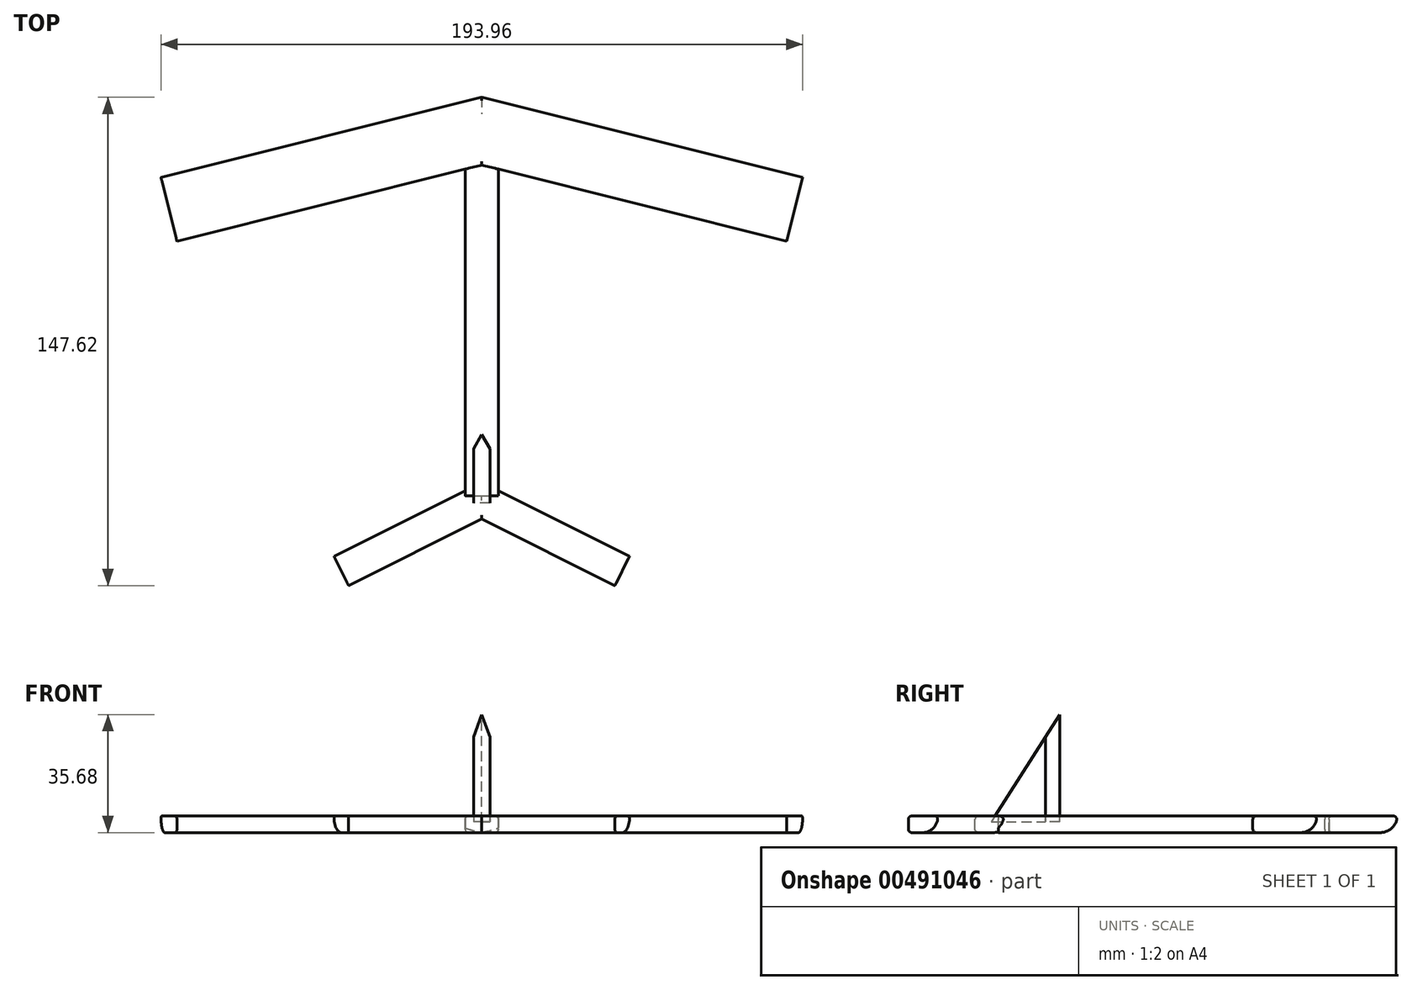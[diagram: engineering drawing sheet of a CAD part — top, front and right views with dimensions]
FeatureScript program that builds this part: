
annotation { "Feature Type Name" : "Feature", "Feature Type Description" : "" }
export const myFeature = defineFeature(function(context is Context, id is Id, definition is map)
    precondition{}
    {
        {
            var Q0;
            Q0=qCreatedBy(makeId("Top.planeOp"),FACE);
            var sketch = newSketch(context, id + "F0", { "sketchPlane" : qUnion([Q0])});
            skLineSegment(sketch, "E0", {"start": v(0, 0) * mm, "end": v(97.01, -24.25) * mm});
            skLineSegment(sketch, "E1", {"start": v(97.01, -24.25) * mm, "end": v(92.16, -43.66) * mm});
            skLineSegment(sketch, "E2", {"start": v(92.16, -43.66) * mm, "end": v(0, -20.62) * mm});
            skLineSegment(sketch, "E3", {"start": v(0, -20.62) * mm, "end": v(0, 0) * mm});
            skPoint(sketch, "E4.start.orphan", {"position": v(-0.68, 0) * mm});
            skLineSegment(sketch, "E5", {"start": v(0, 0) * mm, "end": v(-97.01, -24.25) * mm});
            skLineSegment(sketch, "E6", {"start": v(-97.01, -24.25) * mm, "end": v(-92.16, -43.66) * mm});
            skLineSegment(sketch, "E7", {"start": v(-92.16, -43.66) * mm, "end": v(0, -20.62) * mm});
            skSolve(sketch);
        }
        {
            var Q0;
            Q0=makeQuery(id+"F0.imprint","IMPRINT",FACE,{"disambiguationData":[TD([[makeQuery(id+"F0.imprint","IMPRINT",EDGE,{"derivedFrom":sQuery(id+"F0.wireOp",EDGE,"E0")}),-1.0]])]});
            extrude(context, id + "F1", {"entities" : qUnion([Q0]), "depth" : 5 * mm});
        }
        {
            var Q0;
            Q0=makeQuery(id+"F0.imprint","IMPRINT",FACE,{"disambiguationData":[TD([[makeQuery(id+"F0.imprint","IMPRINT",EDGE,{"derivedFrom":sQuery(id+"F0.wireOp",EDGE,"E3")}),1.0]])]});
            extrude(context, id + "F2", {"entities" : qUnion([Q0]), "operationType" : NewBodyOperationType.ADD, "depth" : 5 * mm});
        }
        {
            var Q0;
            {var subQ0=sQuery(id+"F0.wireOp",EDGE,"E3");Q0=makeQuery(id+"F2.boolean.opBoolean","MERGE",FACE,{"derivedFrom":[makeQuery(id+"F1.opExtrude","CAP_FACE",FACE,{"disambiguationData":[OSD([sQuery(id+"F0.wireOp",EDGE,"E0"),sQuery(id+"F0.wireOp",EDGE,"E1"),sQuery(id+"F0.wireOp",EDGE,"E2"),subQ0])],"isStart":false}),makeQuery(id+"F2.opExtrude","CAP_FACE",FACE,{"disambiguationData":[OSD([subQ0,sQuery(id+"F0.wireOp",EDGE,"E5"),sQuery(id+"F0.wireOp",EDGE,"E6"),sQuery(id+"F0.wireOp",EDGE,"E7")])],"isStart":false})]});}
            var sketch = newSketch(context, id + "F3", { "sketchPlane" : qUnion([Q0])});
            skLineSegment(sketch, "E8.bottom", {"start": v(0, -20.62) * mm, "end": v(-5, -20.62) * mm});
            skLineSegment(sketch, "E8.top", {"start": v(0, -120.62) * mm, "end": v(-5, -120.62) * mm});
            skLineSegment(sketch, "E8.left", {"start": v(0, -20.62) * mm, "end": v(0, -120.62) * mm});
            skLineSegment(sketch, "E8.right", {"start": v(-5, -20.62) * mm, "end": v(-5, -120.62) * mm});
            skLineSegment(sketch, "E9.MirrorCS", {"start": v(5, -20.62) * mm, "end": v(5, -120.62) * mm});
            skLineSegment(sketch, "E10.MirrorCS", {"start": v(0, -20.62) * mm, "end": v(5, -20.62) * mm});
            skLineSegment(sketch, "E11.MirrorCS", {"start": v(0, -120.62) * mm, "end": v(5, -120.62) * mm});
            skSolve(sketch);
        }
        {
            var Q0;
            {var subQ0=sQuery(id+"F3.wireOp",EDGE,"E8.left");Q0=makeQuery(id+"F3.imprint","IMPRINT",FACE,{"disambiguationData":[TD([[makeQuery(id+"F3.imprint","IMPRINT",EDGE,{"derivedFrom":subQ0}),1.0]])]});}
            var Q1;
            {var subQ0=sQuery(id+"F3.wireOp",EDGE,"E8.top");Q1=makeQuery(id+"F3.imprint","IMPRINT",FACE,{"disambiguationData":[TD([[makeQuery(id+"F3.imprint","IMPRINT",EDGE,{"derivedFrom":subQ0}),-1.0]])]});}
            extrude(context, id + "F4", {"entities" : qUnion([Q0, Q1]), "oppositeDirection" : true, "depth" : 5 * mm});
        }
        {
            var Q0;
            Q0=makeQuery(id+"F4.opExtrude","CAP_FACE",FACE,{"disambiguationData":[OSD([sQuery(id+"F0.wireOp",EDGE,"E2"),sQuery(id+"F0.wireOp",EDGE,"E7"),sQuery(id+"F3.wireOp",EDGE,"E8.top"),sQuery(id+"F3.wireOp",EDGE,"E8.right"),sQuery(id+"F3.wireOp",EDGE,"E9.MirrorCS"),sQuery(id+"F3.wireOp",EDGE,"E11.MirrorCS")])],"isStart":true});
            var sketch = newSketch(context, id + "F5", { "sketchPlane" : qUnion([Q0])});
            skLineSegment(sketch, "E12", {"start": v(0, -116.44) * mm, "end": v(-44.72, -138.8) * mm});
            skLineSegment(sketch, "E13", {"start": v(-44.72, -138.8) * mm, "end": v(-40.25, -147.75) * mm});
            skLineSegment(sketch, "E14", {"start": v(-40.25, -147.75) * mm, "end": v(0, -127.63) * mm});
            skLineSegment(sketch, "E15", {"start": v(0, -127.63) * mm, "end": v(0, -116.44) * mm});
            skLineSegment(sketch, "E16.MirrorCS", {"start": v(0, -116.44) * mm, "end": v(44.72, -138.8) * mm});
            skLineSegment(sketch, "E17.MirrorCS", {"start": v(40.25, -147.75) * mm, "end": v(0, -127.63) * mm});
            skLineSegment(sketch, "E18.MirrorCS", {"start": v(44.72, -138.8) * mm, "end": v(40.25, -147.75) * mm});
            skSolve(sketch);
        }
        {
            var Q0;
            {var subQ8=sQuery(id+"F5.wireOp",EDGE,"E13");Q0=makeQuery(id+"F5.imprint","IMPRINT",FACE,{"disambiguationData":[TD([[makeQuery(id+"F5.imprint","IMPRINT",EDGE,{"derivedFrom":subQ8}),1.0]])]});}
            var Q1;
            {var subQ0=sQuery(id+"F5.wireOp",EDGE,"E17.MirrorCS");Q1=makeQuery(id+"F5.imprint","IMPRINT",FACE,{"disambiguationData":[TD([[makeQuery(id+"F5.imprint","IMPRINT",EDGE,{"derivedFrom":subQ0}),-1.0]])]});}
            extrude(context, id + "F6", {"entities" : qUnion([Q0, Q1]), "oppositeDirection" : true, "depth" : 5 * mm});
        }
        {
            var Q0;
            Q0=qCreatedBy(makeId("Right.planeOp"),FACE);
            var sketch = newSketch(context, id + "F7", { "sketchPlane" : qUnion([Q0])});
            skLineSegment(sketch, "E19", {"start": v(-101.37, 5.47) * mm, "end": v(-101.37, 36.73) * mm});
            skLineSegment(sketch, "E20", {"start": v(-101.37, 36.73) * mm, "end": v(-121.14, 5.74) * mm});
            skLineSegment(sketch, "E21", {"start": v(-121.14, 5.74) * mm, "end": v(-122.76, 3.2) * mm});
            skLineSegment(sketch, "E22", {"start": v(-122.76, 3.2) * mm, "end": v(-101.37, 3.2) * mm});
            skLineSegment(sketch, "E23", {"start": v(-101.37, 3.2) * mm, "end": v(-101.37, 5.47) * mm});
            skSolve(sketch);
        }
        {
            var Q0;
            Q0=makeQuery(id+"F7.imprint","IMPRINT",FACE,{"disambiguationData":[TD([[makeQuery(id+"F7.imprint","IMPRINT",EDGE,{"derivedFrom":sQuery(id+"F7.wireOp",EDGE,"E19")}),1.0]])]});
            extrude(context, id + "F8", {"entities" : qUnion([Q0]), "endBound" : BoundingType.SYMMETRIC, "depth" : 5 * mm});
        }
        {
            var Q0;
            Q0=makeQuery(id+"F1.opExtrude","CAP_EDGE",EDGE,{"disambiguationData":[OSD([sQuery(id+"F0.wireOp",EDGE,"E0")])],"isStart":true});
            var Q1;
            Q1=makeQuery(id+"F2.opExtrude","CAP_EDGE",EDGE,{"disambiguationData":[OSD([sQuery(id+"F0.wireOp",EDGE,"E5")])],"isStart":true});
            fillet(context, id + "F9", {"entities" : qUnion([Q0, Q1]), "radius" : 5 * mm, "tangentPropagation" : true, "allowEdgeOverflow" : false});
        }
        {
            var Q0;
            {var subQ0=sQuery(id+"F0.wireOp",EDGE,"E3");var subQ1=sQuery(id+"F0.wireOp",EDGE,"E0");Q0=makeQuery(id+"F9.opFillet","BLEND_EDGE",EDGE,{"blendedFrom":[makeQuery(id+"F1.opExtrude","CAP_EDGE",EDGE,{"disambiguationData":[OSD([subQ1])],"isStart":true}),makeQuery(id+"F2.boolean.opBoolean","MERGE",FACE,{"derivedFrom":[makeQuery(id+"F1.opExtrude","CAP_FACE",FACE,{"disambiguationData":[OSD([subQ1,sQuery(id+"F0.wireOp",EDGE,"E1"),sQuery(id+"F0.wireOp",EDGE,"E2"),subQ0])],"isStart":false}),makeQuery(id+"F2.opExtrude","CAP_FACE",FACE,{"disambiguationData":[OSD([subQ0,sQuery(id+"F0.wireOp",EDGE,"E5"),sQuery(id+"F0.wireOp",EDGE,"E6"),sQuery(id+"F0.wireOp",EDGE,"E7")])],"isStart":false})]})],"blendedInto":[makeQuery(id+"F2.boolean.opBoolean","MERGE",FACE,{"derivedFrom":[makeQuery(id+"F1.opExtrude","CAP_FACE",FACE,{"disambiguationData":[OSD([subQ1,sQuery(id+"F0.wireOp",EDGE,"E1"),sQuery(id+"F0.wireOp",EDGE,"E2"),subQ0])],"isStart":false}),makeQuery(id+"F2.opExtrude","CAP_FACE",FACE,{"disambiguationData":[OSD([subQ0,sQuery(id+"F0.wireOp",EDGE,"E5"),sQuery(id+"F0.wireOp",EDGE,"E6"),sQuery(id+"F0.wireOp",EDGE,"E7")])],"isStart":false})]})]});}
            var Q1;
            {var subQ0=sQuery(id+"F0.wireOp",EDGE,"E5");var subQ1=sQuery(id+"F0.wireOp",EDGE,"E3");Q1=makeQuery(id+"F9.opFillet","BLEND_EDGE",EDGE,{"blendedFrom":[makeQuery(id+"F2.opExtrude","CAP_EDGE",EDGE,{"disambiguationData":[OSD([subQ0])],"isStart":true}),makeQuery(id+"F2.boolean.opBoolean","MERGE",FACE,{"derivedFrom":[makeQuery(id+"F1.opExtrude","CAP_FACE",FACE,{"disambiguationData":[OSD([sQuery(id+"F0.wireOp",EDGE,"E0"),sQuery(id+"F0.wireOp",EDGE,"E1"),sQuery(id+"F0.wireOp",EDGE,"E2"),subQ1])],"isStart":false}),makeQuery(id+"F2.opExtrude","CAP_FACE",FACE,{"disambiguationData":[OSD([subQ1,subQ0,sQuery(id+"F0.wireOp",EDGE,"E6"),sQuery(id+"F0.wireOp",EDGE,"E7")])],"isStart":false})]})],"blendedInto":[makeQuery(id+"F2.boolean.opBoolean","MERGE",FACE,{"derivedFrom":[makeQuery(id+"F1.opExtrude","CAP_FACE",FACE,{"disambiguationData":[OSD([sQuery(id+"F0.wireOp",EDGE,"E0"),sQuery(id+"F0.wireOp",EDGE,"E1"),sQuery(id+"F0.wireOp",EDGE,"E2"),subQ1])],"isStart":false}),makeQuery(id+"F2.opExtrude","CAP_FACE",FACE,{"disambiguationData":[OSD([subQ1,subQ0,sQuery(id+"F0.wireOp",EDGE,"E6"),sQuery(id+"F0.wireOp",EDGE,"E7")])],"isStart":false})]})]});}
            fillet(context, id + "F10", {"entities" : qUnion([Q0, Q1]), "radius" : 1 * mm, "tangentPropagation" : true, "allowEdgeOverflow" : false});
        }
        {
            var Q0;
            Q0=makeQuery(id+"F6.opExtrude","CAP_EDGE",EDGE,{"disambiguationData":[OSD([sQuery(id+"F5.wireOp",EDGE,"E16.MirrorCS")])],"isStart":false});
            var Q1;
            Q1=makeQuery(id+"F6.opExtrude","CAP_EDGE",EDGE,{"disambiguationData":[OSD([sQuery(id+"F5.wireOp",EDGE,"E12")])],"isStart":false});
            fillet(context, id + "F11", {"entities" : qUnion([Q0, Q1]), "radius" : 5 * mm, "tangentPropagation" : true, "allowEdgeOverflow" : false});
        }
        {
            var Q0;
            {var subQ0=sQuery(id+"F5.wireOp",EDGE,"E16.MirrorCS");Q0=makeQuery(id+"F11.opFillet","BLEND_EDGE",EDGE,{"blendedFrom":[makeQuery(id+"F6.opExtrude","CAP_EDGE",EDGE,{"disambiguationData":[OSD([subQ0])],"isStart":false}),makeQuery(id+"F6.opExtrude","CAP_FACE",FACE,{"disambiguationData":[OSD([sQuery(id+"F3.wireOp",EDGE,"E8.top"),sQuery(id+"F3.wireOp",EDGE,"E8.right"),sQuery(id+"F3.wireOp",EDGE,"E9.MirrorCS"),sQuery(id+"F3.wireOp",EDGE,"E11.MirrorCS"),sQuery(id+"F5.wireOp",EDGE,"E12"),sQuery(id+"F5.wireOp",EDGE,"E13"),sQuery(id+"F5.wireOp",EDGE,"E14"),subQ0,sQuery(id+"F5.wireOp",EDGE,"E17.MirrorCS"),sQuery(id+"F5.wireOp",EDGE,"E18.MirrorCS")])],"isStart":true})],"blendedInto":[makeQuery(id+"F6.opExtrude","CAP_FACE",FACE,{"disambiguationData":[OSD([sQuery(id+"F3.wireOp",EDGE,"E8.top"),sQuery(id+"F3.wireOp",EDGE,"E8.right"),sQuery(id+"F3.wireOp",EDGE,"E9.MirrorCS"),sQuery(id+"F3.wireOp",EDGE,"E11.MirrorCS"),sQuery(id+"F5.wireOp",EDGE,"E12"),sQuery(id+"F5.wireOp",EDGE,"E13"),sQuery(id+"F5.wireOp",EDGE,"E14"),subQ0,sQuery(id+"F5.wireOp",EDGE,"E17.MirrorCS"),sQuery(id+"F5.wireOp",EDGE,"E18.MirrorCS")])],"isStart":true})]});}
            var Q1;
            {var subQ0=sQuery(id+"F5.wireOp",EDGE,"E12");Q1=makeQuery(id+"F11.opFillet","BLEND_EDGE",EDGE,{"blendedFrom":[makeQuery(id+"F6.opExtrude","CAP_EDGE",EDGE,{"disambiguationData":[OSD([subQ0])],"isStart":false}),makeQuery(id+"F6.opExtrude","CAP_FACE",FACE,{"disambiguationData":[OSD([sQuery(id+"F3.wireOp",EDGE,"E8.top"),sQuery(id+"F3.wireOp",EDGE,"E8.right"),sQuery(id+"F3.wireOp",EDGE,"E9.MirrorCS"),sQuery(id+"F3.wireOp",EDGE,"E11.MirrorCS"),subQ0,sQuery(id+"F5.wireOp",EDGE,"E13"),sQuery(id+"F5.wireOp",EDGE,"E14"),sQuery(id+"F5.wireOp",EDGE,"E16.MirrorCS"),sQuery(id+"F5.wireOp",EDGE,"E17.MirrorCS"),sQuery(id+"F5.wireOp",EDGE,"E18.MirrorCS")])],"isStart":true})],"blendedInto":[makeQuery(id+"F6.opExtrude","CAP_FACE",FACE,{"disambiguationData":[OSD([sQuery(id+"F3.wireOp",EDGE,"E8.top"),sQuery(id+"F3.wireOp",EDGE,"E8.right"),sQuery(id+"F3.wireOp",EDGE,"E9.MirrorCS"),sQuery(id+"F3.wireOp",EDGE,"E11.MirrorCS"),subQ0,sQuery(id+"F5.wireOp",EDGE,"E13"),sQuery(id+"F5.wireOp",EDGE,"E14"),sQuery(id+"F5.wireOp",EDGE,"E16.MirrorCS"),sQuery(id+"F5.wireOp",EDGE,"E17.MirrorCS"),sQuery(id+"F5.wireOp",EDGE,"E18.MirrorCS")])],"isStart":true})]});}
            fillet(context, id + "F12", {"entities" : qUnion([Q0, Q1]), "radius" : 1 * mm, "tangentPropagation" : true, "allowEdgeOverflow" : false});
        }
        {
            var Q0;
            Q0=makeQuery(id+"F8.opExtrude","CAP_EDGE",EDGE,{"disambiguationData":[OSD([sQuery(id+"F7.wireOp",EDGE,"E19"),sQuery(id+"F7.wireOp",EDGE,"E23")])],"isStart":false});
            var Q1;
            Q1=makeQuery(id+"F8.opExtrude","CAP_EDGE",EDGE,{"disambiguationData":[OSD([sQuery(id+"F7.wireOp",EDGE,"E19"),sQuery(id+"F7.wireOp",EDGE,"E23")])],"isStart":true});
            chamfer(context, id + "F13", {"entities" : qUnion([Q0, Q1]), "chamferType" : ChamferType.OFFSET_ANGLE, "width" : 5 * mm, "oppositeDirection" : false, "angle" : 30 * degree, "tangentPropagation" : true});
        }
        {
            var Q0;
            Q0=makeQuery(id+"F4.opExtrude","CAP_EDGE",EDGE,{"disambiguationData":[OSD([sQuery(id+"F3.wireOp",EDGE,"E9.MirrorCS")])],"isStart":false});
            var Q1;
            Q1=makeQuery(id+"F4.opExtrude","CAP_EDGE",EDGE,{"disambiguationData":[OSD([sQuery(id+"F3.wireOp",EDGE,"E9.MirrorCS")])],"isStart":true});
            var Q2;
            Q2=makeQuery(id+"F4.opExtrude","CAP_EDGE",EDGE,{"disambiguationData":[OSD([sQuery(id+"F3.wireOp",EDGE,"E8.right")])],"isStart":false});
            var Q3;
            Q3=makeQuery(id+"F4.opExtrude","CAP_EDGE",EDGE,{"disambiguationData":[OSD([sQuery(id+"F3.wireOp",EDGE,"E8.right")])],"isStart":true});
            fillet(context, id + "F14", {"entities" : qUnion([Q0, Q1, Q2, Q3]), "radius" : 1 * mm, "tangentPropagation" : true, "allowEdgeOverflow" : false});
        }
        {
            var Q0;
            Q0=makeQuery(id+"F2.opExtrude","CAP_EDGE",EDGE,{"disambiguationData":[OSD([sQuery(id+"F0.wireOp",EDGE,"E7")])],"isStart":false});
            var Q1;
            Q1=makeQuery(id+"F2.opExtrude","CAP_EDGE",EDGE,{"disambiguationData":[OSD([sQuery(id+"F0.wireOp",EDGE,"E7")])],"isStart":true});
            var Q2;
            Q2=makeQuery(id+"F1.opExtrude","CAP_EDGE",EDGE,{"disambiguationData":[OSD([sQuery(id+"F0.wireOp",EDGE,"E2")])],"isStart":false});
            var Q3;
            Q3=makeQuery(id+"F1.opExtrude","CAP_EDGE",EDGE,{"disambiguationData":[OSD([sQuery(id+"F0.wireOp",EDGE,"E2")])],"isStart":true});
            var Q4;
            Q4=makeQuery(id+"F6.opExtrude","CAP_EDGE",EDGE,{"disambiguationData":[OSD([sQuery(id+"F5.wireOp",EDGE,"E14")])],"isStart":true});
            var Q5;
            Q5=makeQuery(id+"F6.opExtrude","CAP_EDGE",EDGE,{"disambiguationData":[OSD([sQuery(id+"F5.wireOp",EDGE,"E14")])],"isStart":false});
            var Q6;
            Q6=makeQuery(id+"F6.opExtrude","CAP_EDGE",EDGE,{"disambiguationData":[OSD([sQuery(id+"F5.wireOp",EDGE,"E17.MirrorCS")])],"isStart":true});
            var Q7;
            Q7=makeQuery(id+"F6.opExtrude","CAP_EDGE",EDGE,{"disambiguationData":[OSD([sQuery(id+"F5.wireOp",EDGE,"E17.MirrorCS")])],"isStart":false});
            fillet(context, id + "F15", {"entities" : qUnion([Q0, Q1, Q2, Q3, Q4, Q5, Q6, Q7]), "radius" : 1 * mm, "tangentPropagation" : true, "allowEdgeOverflow" : false});
        }
    });
